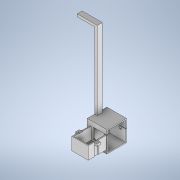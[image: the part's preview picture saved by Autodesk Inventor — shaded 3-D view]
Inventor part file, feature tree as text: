
AUTODESK INVENTOR PART (.ipt)
format: ipt  version: 2020.2 (Build 242310000, 310)  size: 563,200 bytes
history: native  units: mm
features: sketch x25, extrude x24, projected_geometry x8, hole x1
ambient origin geometry x8: Origin, YZ Plane, XZ Plane, XY Plane, X Axis, Y Axis, Z Axis, Center Point
bodies: Solid1 (feature_tree)
feature tree (58):
  sketch  "Sketch1"  dims[d0=29.0mm d1=35.0mm]
  extrude  "Extrusion1"  Depth=35.0mm
  extrude  "Extrusion2"  Depth=2.0mm
  extrude  "Extrusion3"  Depth=39.0mm
  hole  "Hole1"  [1 undecoded]
  extrude  "Extrusion4"  Depth=10.0mm
  sketch  "Sketch5"  dims[d10=10.0mm d11=0.0mm d12=4.2mm]
  sketch  "Sketch6"  dims[d13=4.475mm d14=26.05mm]
  extrude  "Extrusion5"  Depth=26.05mm
  extrude  "Extrusion6"  Depth=39.0mm
  extrude  "Extrusion7"  Depth=33.0mm TaperAngle=0.0deg
  sketch  "Sketch10"  dims[d27=7.0mm d28=7.0mm]
  extrude  "Extrusion8"  Depth=7.0mm
  extrude  "Extrusion9"  Depth=7.0mm
  extrude  "Extrusion14"  Depth=10.0mm
  extrude  "Extrusion15"  Depth=20.0mm
  extrude  "Extrusion16"  Depth=22.5mm
  extrude  "Extrusion17"  Depth=1.0mm
  extrude  "Extrusion18"  Depth=24.0mm
  extrude  "Extrusion19"  Depth=1.0mm
  extrude  "Extrusion25"  Depth=26.0mm
  extrude  "Extrusion26"  Depth=1.0mm
  extrude  "Extrusion27"  Depth=1.0mm
  extrude  "Extrusion21"  Depth=26.0mm TaperAngle=0.0deg
  extrude  "Extrusion22"  Depth=1.0mm TaperAngle=0.0deg
  extrude  "Extrusion23"  Depth=14.0mm
  extrude  "Extrusion24"  TaperAngle=90.0deg  [1 undecoded]
  extrude  "Extrusion28"  Depth=3.5mm
  extrude  "Extrusion29"  Depth=7.0mm
  sketch  "Sketch2"  dims[d2=2.0mm d3=2.0mm]
  sketch  "Sketch3"  dims[d4=33.0mm d5=39.0mm]
  sketch  "Sketch4"  dims[d6=2.0mm d7=0.0mm d8=40.0mm d9=0.0mm]
  sketch  "Sketch7"  dims[d15=29.6mm]
  projected_geometry  "Projected Loop1"
  sketch  "Sketch8"  dims[d16=3.4mm d17=6.0mm d18=6.3mm d19=2.0mm d20=90.0deg d21=8.0mm d22=20.594885mm d23=39.0mm]
  sketch  "Sketch9"  dims[d24=2.0mm d25=33.0mm d26=0.0mm]
  sketch  "Sketch11"  dims[d29=7.0mm d30=7.0mm]
  sketch  "Sketch16"  dims[d31=5.0mm d32=0.0mm d33=10.0mm]
  sketch  "Sketch17"  dims[d34=3.5mm d35=20.0mm]
  sketch  "Sketch18"  dims[d36=90.0deg d37=22.5mm]
  projected_geometry  "Projected Loop4"
  sketch  "Sketch19"  dims[d38=10.0mm d39=0.0mm d40=1.0mm]
  projected_geometry  "Projected Loop5"
  sketch  "Sketch21"  dims[d41=10.0mm d42=0.0mm d43=24.0mm]
  projected_geometry  "Projected Loop6"
  sketch  "Sketch25"  dims[d44=30.48mm d45=1.0mm]
  sketch  "Sketch26"  dims[d46=31.48mm d47=26.0mm]
  sketch  "Sketch27"  dims[d48=34.0mm d49=0.0mm d50=1.0mm]
  sketch  "Sketch28"  dims[d51=29.48mm d52=0.0mm d69=1.0mm]
  sketch  "Sketch30"  dims[d70=35.0mm d71=26.0mm d72=0.0mm]
  projected_geometry  "Projected Loop7"
  sketch  "Sketch31"  dims[d73=10.0mm d74=0.0mm d75=1.0mm d76=0.0mm]
  projected_geometry  "Projected Loop8"
  sketch  "Sketch32"  dims[d77=1.0mm d78=0.0mm d79=14.0mm]
  projected_geometry  "Projected Loop9"
  projected_geometry  "Projected Loop10"
  sketch  "Sketch34"  dims[d80=17.5mm d81=90.0deg]
  sketch  "Sketch35"  dims[d82=35.0mm d83=3.5mm d84=7.0mm d85=7.0mm d86=7.0mm d87=3.4mm d88=3.4mm d89=5.0mm d90=0.0mm d91=1.0mm d92=0.0mm d118=15.0mm d119=10.0mm d120=5.0mm d121=12.7mm d122=0.0mm d123=5.0mm d124=35.0mm d125=0.0mm d126=154.9042mm d127=0.0mm d128=5.0mm d129=35.0mm d130=0.0mm d131=1.0mm d132=0.0mm d133=1.0mm d134=0.0mm d135=1.0mm d136=0.0mm d137=1.0mm d138=0.0mm d139=16.0mm d140=10.0mm d141=1.5mm d142=2.0mm d143=5.0mm d144=3.5mm d145=5.5mm d146=10.0mm d147=0.0mm d54=0.5mm d55=0.872665mm d56=0.5mm d57=0.872665mm d58=0.5mm d59=0.872665mm d60=0.5mm d61=0.872665mm d116=0.5mm d117=0.872665mm]
note: 2 required parameter values undecoded (feature->parameter linkage not recoverable at this tier; creation-order binding heuristic only, values carry confidence <= 0.55)
